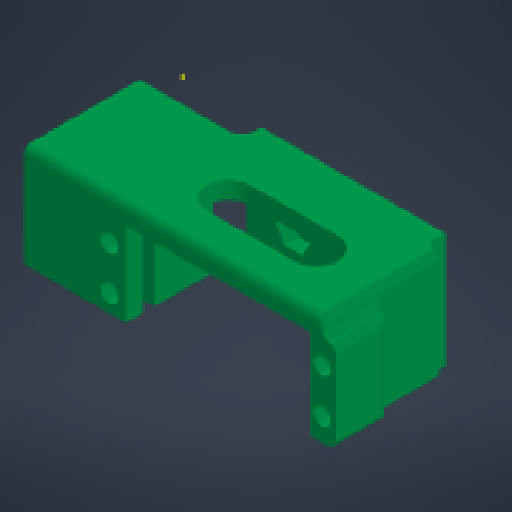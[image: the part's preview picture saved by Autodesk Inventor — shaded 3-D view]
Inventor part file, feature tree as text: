
AUTODESK INVENTOR PART (.ipt)
format: ipt  version: 2024 (Build 280153000, 153)  size: 351,232 bytes
history: native  units: mm
features: sketch x17, extrude x16, other x7, fillet x5, reference x5, projected_geometry x1
ambient origin geometry x8: Origin, YZ Plane, XZ Plane, XY Plane, X Axis, Y Axis, Z Axis, Center Point
bodies: Body1 (feature_tree)
feature tree (51):
  other  "Твердое тело1"
  extrude  "Выдавливание1"  Depth=17.0mm
  extrude  "Выдавливание2"  Depth=17.0mm
  extrude  "Выдавливание5"  Depth=2.0mm
  extrude  "Выдавливание3"  Depth=10.0mm TaperAngle=0.0deg
  extrude  "Выдавливание6"  Depth=1.5mm
  sketch  "Эскиз7"
  other  "РабПлоскость1"
  extrude  "Выдавливание7"  Depth=4.0mm TaperAngle=0.0deg
  extrude  "Выдавливание8"  Depth=10.0mm
  extrude  "Выдавливание9"  Depth=8.0mm
  extrude  "Выдавливание10"  Depth=19.5mm TaperAngle=0.0deg
  fillet  "Сопряжение2"  Radius=19.25mm
  extrude  "Выдавливание11"  Depth=3.0mm
  extrude  "Выдавливание12"  Depth=3.0mm
  extrude  "Выдавливание13"  Depth=4.0mm
  extrude  "Выдавливание14"  Depth=20.0mm
  extrude  "Выдавливание15"  Depth=38.0mm TaperAngle=0.0deg
  sketch  "Эскиз16"
  extrude  "Выдавливание16"  Depth=3.0mm
  fillet  "Сопряжение3"  Radius=27.25mm
  fillet  "Сопряжение4"  Radius=20.5mm
  fillet  "Сопряжение5"  Radius=3.0mm
  fillet  "Сопряжение6"  Radius=12.0mm
  extrude  "Выдавливание17"  Depth=6.5mm TaperAngle=0.0deg
  sketch  "Эскиз1"
  sketch  "Эскиз2"
  sketch  "Эскиз3"
  sketch  "Эскиз5"
  sketch  "Эскиз6"
  projected_geometry  "Спроецированная петля1"
  sketch  "Эскиз8"
  sketch  "Эскиз9"
  reference  "Ссылка3"
  reference  "Ссылка4"
  sketch  "Эскиз10"
  reference  "Ссылка5"
  reference  "Ссылка6"
  sketch  "Эскиз11"
  sketch  "Эскиз12"
  sketch  "Эскиз13"
  sketch  "Эскиз14"
  sketch  "Эскиз15"
  reference  "Ссылка7"
  sketch  "Эскиз17"
  sketch  "Эскиз18"
  parser-record x1  (decoder bookkeeping rows leaked as tree rows — omitted from the tree; the rows remain in map.json)
  other  "manipulator_asembly.iam"
  other  "MG996R SBORKA:1"
  other  "Servo MG996R:1"
  other  "Servo MG996R arm01:1"
note: 1 file-system path scrubbed to <path> (originals preserved in map.json)
